# Revit family: NBS_DudleyIndustriesLimited_SoapDpnsrs_ModuloManualSoap
name_source: partatom
category: Generic Models
revit_build: Autodesk Revit 2017 (Build: 20171027_0315(x64)
units: mm (PartAtom-declared; Revit-internal decimal feet)

## family parameters
Always vertical = Yes
Can host rebar = No
Cut with Voids When Loaded = No
Part Type = Normal
Room Calculation Point = No
Round Connector Dimension = Use Diameter
Shared = No
Work Plane-Based = No

## types (1)
- ModuloManualSoap
    AssetType = Fixed
    BIMObjectName = NBS_DudleyIndustriesLimited_SoapDispensers_ModuloManualSoap
    Category = Pr_40_70_22_81:Soap dispensers
    Color = Black
    Description = Soap dispenser for effective hand cleaning, pull lever, visible below the cabinet dispensers liquid soap in, palm of hand
    DurationUnit = year
    ExpectedLife = 10
    Features = Fits the modulo behind the mirror system, reservoir is quick and easy to refill, large 1L capacity for busy washrooms, dispensing pump compatible with most liquid soap formulations, spare consumables can be conveniently stored on the shelf within the cabinet, consumables not accessible and kept free from contamination by lockable cabinet cover, lever presented to user under the cabinet with clear instructions for use, lever protrudes 80mm under cabinet, no batteries required, utilises half a modular cabinet space, blanking plates available separately if required
    Finish = Matte black powder coated
    Form = Fits the modulo behind the mirror system
    Grade = Stainless Steel, EN1.4509
    IfcExportAs = IfcFurnitureType
    IfcExportType = NOTDEFINED
    IsBuiltIn = Yes
    ManufacturerName = Dudley Industries Limited
    ManufacturerURL = https://www.dudleyindustries.com
    Material = Stainless steel
    MaterialsBody = Stainless steel
    MaterialsFinishAndColour = Matte black powder coated
    ModelNumber = 92370BK
    ModelReference = Modulo Manual Soap
    NBSCertification = www.nationalbimlibrary.com/cert/ahx1gfc4
    NBSDescription = Soap dispensers
    NBSReference = 45-35-72/358
    Name = SoapDispensers_ModuloManualSoap_DudleyIndustriesLimited
    NominalDepth = 193 mm  [stored 0.633202 ft]
    NominalHeight = 280 mm
    NominalLength = 193 mm  [stored 0.633202 ft]
    NominalWidth = 193 mm  [stored 0.633202 ft]
    Operation = Manual
    Size = 193 x 280 x 193 mm
    SoapDispenserMaterial = NBS_Concept
    Status = New
    Style = Soap dispensers
    Uniclass2015Code = Pr_40_70_22_81
    Uniclass2015Title = Soap dispensers
    Uniclass2015Version = Products v1.12
    Version = 1
    WarrantyDescription = 10 year warranty
    WarrantyDurationUnit = year

note: [stored X ft] marks values corroborated as IEEE doubles in the binary element streams (Revit-internal decimal feet)

## geometry (parser evidence)
native form markers: Sweep x2
no freeform markers — native parametric forms only
